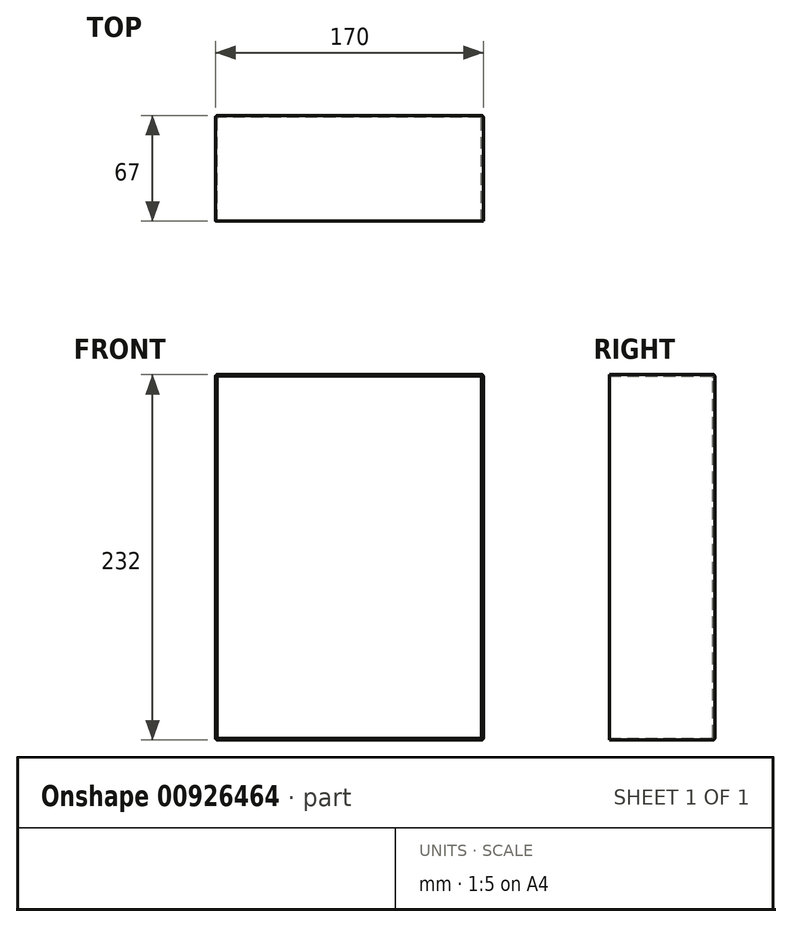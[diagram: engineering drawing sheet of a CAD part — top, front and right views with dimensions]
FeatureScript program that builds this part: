
annotation { "Feature Type Name" : "Feature", "Feature Type Description" : "" }
export const myFeature = defineFeature(function(context is Context, id is Id, definition is map)
    precondition{}
    {
        {
            var Q0;
            Q0=qCreatedBy(makeId("Front.planeOp"),FACE);
            var sketch = newSketch(context, id + "F0", { "sketchPlane" : qUnion([Q0])});
            skLineSegment(sketch, "E0.bottom", {"start": v(85, -116) * mm, "end": v(-85, -116) * mm});
            skLineSegment(sketch, "E0.top", {"start": v(85, 116) * mm, "end": v(-85, 116) * mm});
            skLineSegment(sketch, "E0.left", {"start": v(85, -116) * mm, "end": v(85, 116) * mm});
            skLineSegment(sketch, "E0.right", {"start": v(-85, -116) * mm, "end": v(-85, 116) * mm});
            skPoint(sketch, "E0.middle", {"position": v(0, 0) * mm});
            skSolve(sketch);
        }
        {
            var Q0;
            Q0=makeQuery(id+"F0.imprint","IMPRINT",FACE,{"disambiguationData":[TD([[makeQuery(id+"F0.imprint","IMPRINT",EDGE,{"derivedFrom":sQuery(id+"F0.wireOp",EDGE,"E0.bottom")}),-1.0]])]});
            extrude(context, id + "F1", {"entities" : qUnion([Q0]), "depth" : 67 * mm, "offsetDistance" : 25 * mm});
        }
        {
            var Q0;
            Q0=makeQuery(id+"F1.opExtrude","CAP_FACE",FACE,{"disambiguationData":[OSD([sQuery(id+"F0.wireOp",EDGE,"E0.bottom"),sQuery(id+"F0.wireOp",EDGE,"E0.top"),sQuery(id+"F0.wireOp",EDGE,"E0.left"),sQuery(id+"F0.wireOp",EDGE,"E0.right")])],"isStart":false});
            shell(context, id + "F2", {"entities" : qUnion([Q0]), "thickness" : 1 * mm});
        }
        {
            var Q0;
            Q0=makeQuery(id+"F1.opExtrude","SWEPT_EDGE",EDGE,{"disambiguationData":[OSD([sQuery(id+"F0.wireOp",EDGE,"E0.bottom"),sQuery(id+"F0.wireOp",EDGE,"E0.left")])]});
            var Q1;
            Q1=makeQuery(id+"F1.opExtrude","SWEPT_EDGE",EDGE,{"disambiguationData":[OSD([sQuery(id+"F0.wireOp",EDGE,"E0.top"),sQuery(id+"F0.wireOp",EDGE,"E0.left")])]});
            var Q2;
            Q2=makeQuery(id+"F1.opExtrude","CAP_EDGE",EDGE,{"disambiguationData":[OSD([sQuery(id+"F0.wireOp",EDGE,"E0.left")])],"isStart":true});
            var Q3;
            Q3=makeQuery(id+"F1.opExtrude","CAP_EDGE",EDGE,{"disambiguationData":[OSD([sQuery(id+"F0.wireOp",EDGE,"E0.bottom")])],"isStart":true});
            var Q4;
            Q4=makeQuery(id+"F1.opExtrude","CAP_EDGE",EDGE,{"disambiguationData":[OSD([sQuery(id+"F0.wireOp",EDGE,"E0.right")])],"isStart":true});
            var Q5;
            Q5=makeQuery(id+"F1.opExtrude","SWEPT_EDGE",EDGE,{"disambiguationData":[OSD([sQuery(id+"F0.wireOp",EDGE,"E0.bottom"),sQuery(id+"F0.wireOp",EDGE,"E0.right")])]});
            var Q6;
            Q6=makeQuery(id+"F1.opExtrude","SWEPT_EDGE",EDGE,{"disambiguationData":[OSD([sQuery(id+"F0.wireOp",EDGE,"E0.top"),sQuery(id+"F0.wireOp",EDGE,"E0.right")])]});
            var Q7;
            Q7=makeQuery(id+"F1.opExtrude","CAP_EDGE",EDGE,{"disambiguationData":[OSD([sQuery(id+"F0.wireOp",EDGE,"E0.top")])],"isStart":true});
            var Q8;
            Q8=makeQuery(id+"F2.opShell","OFFSET_EDGE",EDGE,{"disambiguationData":[OSD([sQuery(id+"F0.wireOp",EDGE,"E0.top"),sQuery(id+"F0.wireOp",EDGE,"E0.left")])]});
            var Q9;
            Q9=makeQuery(id+"F2.opShell","OFFSET_FACE",FACE,{"disambiguationData":[OSD([sQuery(id+"F0.wireOp",EDGE,"E0.bottom"),sQuery(id+"F0.wireOp",EDGE,"E0.top"),sQuery(id+"F0.wireOp",EDGE,"E0.left"),sQuery(id+"F0.wireOp",EDGE,"E0.right")])]});
            var Q10;
            Q10=makeQuery(id+"F2.opShell","OFFSET_EDGE",EDGE,{"disambiguationData":[OSD([sQuery(id+"F0.wireOp",EDGE,"E0.bottom"),sQuery(id+"F0.wireOp",EDGE,"E0.left")])]});
            var Q11;
            Q11=makeQuery(id+"F2.opShell","OFFSET_EDGE",EDGE,{"disambiguationData":[OSD([sQuery(id+"F0.wireOp",EDGE,"E0.top"),sQuery(id+"F0.wireOp",EDGE,"E0.right")])]});
            fillet(context, id + "F3", {"entities" : qUnion([Q0, Q1, Q2, Q3, Q4, Q5, Q6, Q7, Q8, Q9, Q10, Q11]), "radius" : 1 * mm, "tangentPropagation" : true, "allowEdgeOverflow" : false});
        }
    });
